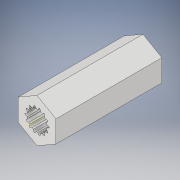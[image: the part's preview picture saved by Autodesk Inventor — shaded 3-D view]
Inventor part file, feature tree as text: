
AUTODESK INVENTOR PART (.ipt)
format: ipt  version: 2019 (Build 230136000, 136)  size: 558,592 bytes
history: native  units: in
note: dims shown in document units (in); Inventor stores cm internally (conversion verified against a paired STEP export)
features: extrude x3, sketch x3, projected_geometry x1, other x1
ambient origin geometry x8: Origin, YZ Plane, XZ Plane, XY Plane, X Axis, Y Axis, Z Axis, Center Point
bodies: Solid1 (feature_tree)
feature tree (8):
  extrude  "Extrusion1"  TaperAngle=0.0deg  [1 undecoded]
  extrude  "Extrusion2"  Depth=1.375in TaperAngle=0.0deg
  extrude  "Extrusion3"  [1 undecoded]
  sketch  "Sketch1"  dims[d1=0.49in d2=0.0in d3=0.0in]
  sketch  "Sketch2"  dims[d4=0.0in d5=0.0in d6=1.375in d7=0.0in]
  sketch  "Sketch3"
  projected_geometry  "Projected Loop1"
  other  "Boss-Extrude2"
note: 2 required parameter values undecoded (feature->parameter linkage not recoverable at this tier; creation-order binding heuristic only, values carry confidence <= 0.55)
